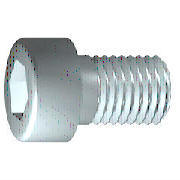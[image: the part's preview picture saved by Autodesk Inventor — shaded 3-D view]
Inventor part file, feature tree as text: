
AUTODESK INVENTOR PART (.ipt)
format: ipt  version: 2015 (Build 190159000, 159)  size: 192,512 bytes
history: native  units: mm (DEFAULTED — no unit token found)
features: sketch x2, extrude x1, plane x1, fillet x1
ambient origin geometry x7: Origin, YZ Plane, XY Plane, X Axis, Y Axis, Z Axis, Center Point
bodies: Solid1 (feature_tree), Body (feature_tree)
feature tree (5):
  extrude  "Slot"  Depth=2.5mm
  plane  "Work Plane1"
  fillet  "Fillet2"  Radius=2.5mm
  sketch  "Sketch1"  dims[d1=4.875mm d2=0.276153mm d3=2.5mm]
  sketch  "Sketch2"  dims[d4=1.1mm d5=60.0deg d6=2.5mm d7=2.5mm d8=2.309401mm d9=4.5mm d10=90.0deg d11=10.0mm d12=0.0mm d13=4.875mm d14=0.0mm d15=0.276052mm d16=0.276053mm d17=0.25mm d19=0.0mm d26=6.0mm d27=45.0deg d28=0.0mm d29=0.0mm d30=0.1mm]
